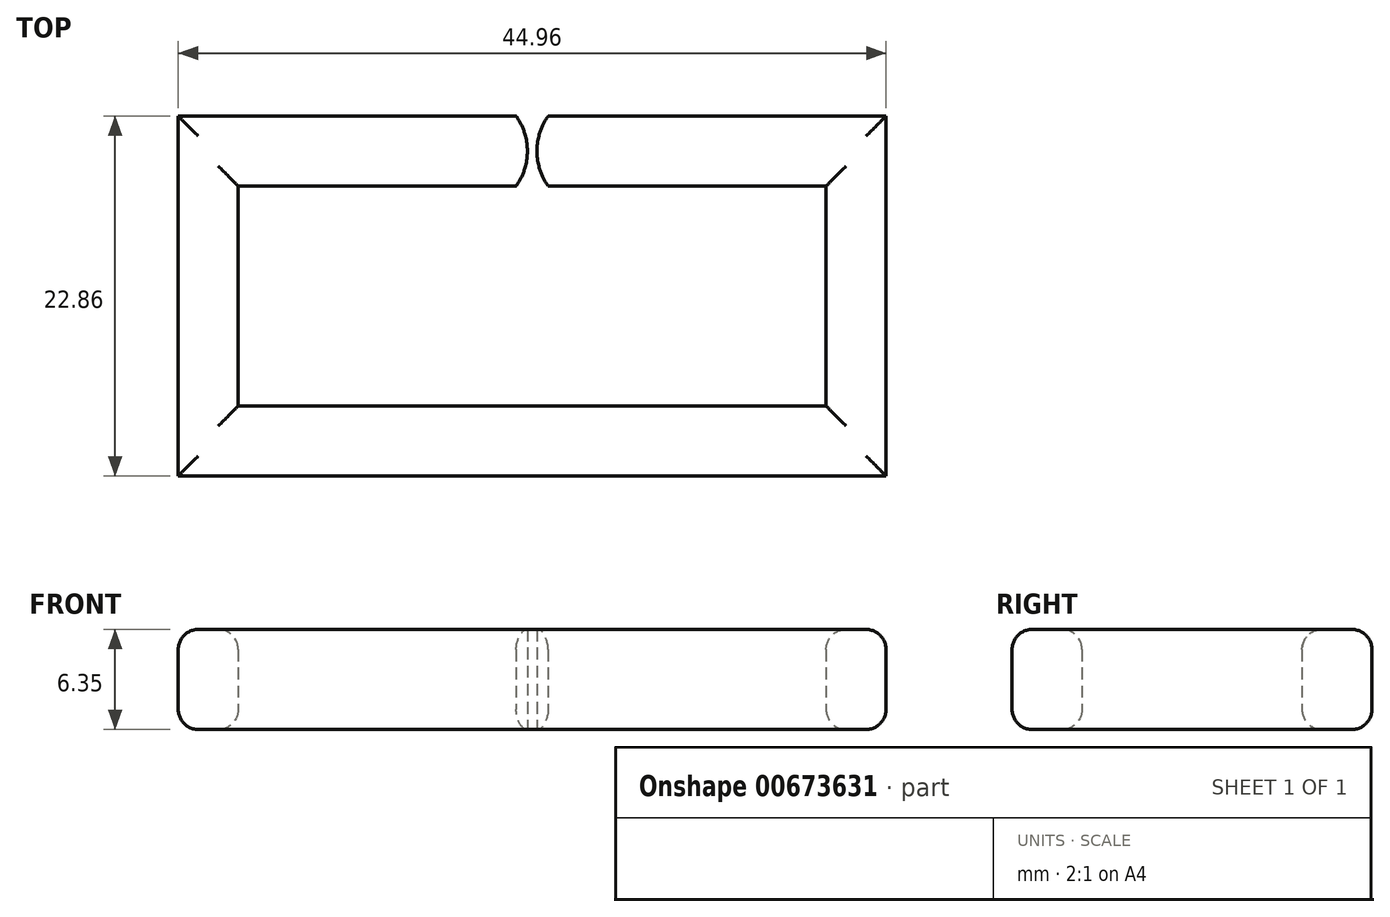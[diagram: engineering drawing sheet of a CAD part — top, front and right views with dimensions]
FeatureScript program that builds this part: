
annotation { "Feature Type Name" : "Feature", "Feature Type Description" : "" }
export const myFeature = defineFeature(function(context is Context, id is Id, definition is map)
    precondition{}
    {
        {
            var Q0;
            Q0=qCreatedBy(makeId("Top.planeOp"),FACE);
            var sketch = newSketch(context, id + "F0", { "sketchPlane" : qUnion([Q0])});
            skLineSegment(sketch, "E0.bottom", {"start": v(22.48, -11.43) * mm, "end": v(-22.48, -11.43) * mm});
            skLineSegment(sketch, "E0.top", {"start": v(22.48, 11.43) * mm, "end": v(-22.48, 11.43) * mm});
            skLineSegment(sketch, "E0.left", {"start": v(22.48, -11.43) * mm, "end": v(22.48, 11.43) * mm});
            skLineSegment(sketch, "E0.right", {"start": v(-22.48, -11.43) * mm, "end": v(-22.48, 11.43) * mm});
            skPoint(sketch, "E0.middle", {"position": v(0, 0) * mm});
            skLineSegment(sketch, "E1.bottom", {"start": v(-18.67, -6.99) * mm, "end": v(18.67, -6.99) * mm});
            skLineSegment(sketch, "E1.top", {"start": v(-18.67, 6.99) * mm, "end": v(18.67, 6.99) * mm});
            skLineSegment(sketch, "E1.left", {"start": v(-18.67, -6.99) * mm, "end": v(-18.67, 6.99) * mm});
            skLineSegment(sketch, "E1.right", {"start": v(18.67, -6.99) * mm, "end": v(18.67, 6.99) * mm});
            skLineSegment(sketch, "E2", {"start": v(0, 6.99) * mm, "end": v(0, 11.43) * mm});
            skLineSegment(sketch, "E3", {"start": v(-1.02, 11.43) * mm, "end": v(-1.02, 6.99) * mm});
            skLineSegment(sketch, "E4.MirrorCS", {"start": v(1.02, 11.43) * mm, "end": v(1.02, 6.99) * mm});
            skLineSegment(sketch, "E5.MirrorCS", {"start": v(0, 11.43) * mm, "end": v(1.02, 11.43) * mm});
            skArc(sketch, "E6", {"start": v(-1.02, 6.99) * mm, "mid": v(-0.3, 9.2) * mm, "end": v(-1.02, 11.43) * mm});
            skArc(sketch, "E7", {"start": v(1.02, 11.43) * mm, "mid": v(0.3, 9.2) * mm, "end": v(1.02, 6.99) * mm});
            skPoint(sketch, "E7.midSnap0", {"position": v(1.02, 9.2) * mm});
            skPoint(sketch, "E7.midSnap1", {"position": v(0.5, 11.43) * mm});
            skSolve(sketch);
        }
        {
            var Q0;
            Q0=makeQuery(id+"F0.imprint","IMPRINT",FACE,{"disambiguationData":[TD([[makeQuery(id+"F0.imprint","IMPRINT",EDGE,{"derivedFrom":sQuery(id+"F0.wireOp",EDGE,"E0.bottom")}),-1.0]])]});
            var Q1;
            Q1=makeQuery(id+"F0.imprint","IMPRINT",FACE,{"disambiguationData":[TD([[makeQuery(id+"F0.imprint","IMPRINT",EDGE,{"derivedFrom":sQuery(id+"F0.wireOp",EDGE,"E3")}),1.0]])]});
            var Q2;
            Q2=makeQuery(id+"F0.imprint","IMPRINT",FACE,{"disambiguationData":[TD([[makeQuery(id+"F0.imprint","IMPRINT",EDGE,{"derivedFrom":sQuery(id+"F0.wireOp",EDGE,"E4.MirrorCS")}),-1.0]])]});
            extrude(context, id + "F1", {"entities" : qUnion([Q0, Q1, Q2]), "depth" : 6.35 * mm, "offsetDistance" : 25.4 * mm});
        }
        {
            var Q0;
            {var subQ0=sQuery(id+"F0.wireOp",EDGE,"E1.top");Q0=makeQuery(id+"F1.opExtrude","CAP_EDGE",EDGE,{"disambiguationData":[OSD([subQ0]),TDD([makeQuery(id+"F0.imprint","IMPRINT",EDGE,{"disambiguationData":[TD([[makeQuery(id+"F0.imprint","INTERSECT",VERTEX,{"derivedFrom":[subQ0,sQuery(id+"F0.wireOp",EDGE,"E1.left")]}),-1.0]])],"derivedFrom":subQ0})])],"isStart":false});}
            var Q1;
            {var subQ0=sQuery(id+"F0.wireOp",EDGE,"E1.top");Q1=makeQuery(id+"F1.opExtrude","CAP_EDGE",EDGE,{"disambiguationData":[OSD([subQ0]),TDD([makeQuery(id+"F0.imprint","IMPRINT",EDGE,{"disambiguationData":[TD([[makeQuery(id+"F0.imprint","INTERSECT",VERTEX,{"derivedFrom":[subQ0,sQuery(id+"F0.wireOp",EDGE,"E1.right")]}),1.0]])],"derivedFrom":subQ0})])],"isStart":false});}
            var Q2;
            Q2=makeQuery(id+"F1.opExtrude","CAP_EDGE",EDGE,{"disambiguationData":[OSD([sQuery(id+"F0.wireOp",EDGE,"E1.right")])],"isStart":false});
            var Q3;
            Q3=makeQuery(id+"F1.opExtrude","CAP_EDGE",EDGE,{"disambiguationData":[OSD([sQuery(id+"F0.wireOp",EDGE,"E1.bottom")])],"isStart":false});
            var Q4;
            Q4=makeQuery(id+"F1.opExtrude","CAP_EDGE",EDGE,{"disambiguationData":[OSD([sQuery(id+"F0.wireOp",EDGE,"E1.left")])],"isStart":false});
            var Q5;
            Q5=makeQuery(id+"F1.opExtrude","CAP_EDGE",EDGE,{"disambiguationData":[OSD([sQuery(id+"F0.wireOp",EDGE,"E1.bottom")])],"isStart":true});
            var Q6;
            Q6=makeQuery(id+"F1.opExtrude","CAP_EDGE",EDGE,{"disambiguationData":[OSD([sQuery(id+"F0.wireOp",EDGE,"E1.right")])],"isStart":true});
            var Q7;
            {var subQ0=sQuery(id+"F0.wireOp",EDGE,"E1.top");Q7=makeQuery(id+"F1.opExtrude","CAP_EDGE",EDGE,{"disambiguationData":[OSD([subQ0]),TDD([makeQuery(id+"F0.imprint","IMPRINT",EDGE,{"disambiguationData":[TD([[makeQuery(id+"F0.imprint","INTERSECT",VERTEX,{"derivedFrom":[subQ0,sQuery(id+"F0.wireOp",EDGE,"E1.right")]}),1.0]])],"derivedFrom":subQ0})])],"isStart":true});}
            var Q8;
            {var subQ0=sQuery(id+"F0.wireOp",EDGE,"E1.top");Q8=makeQuery(id+"F1.opExtrude","CAP_EDGE",EDGE,{"disambiguationData":[OSD([subQ0]),TDD([makeQuery(id+"F0.imprint","IMPRINT",EDGE,{"disambiguationData":[TD([[makeQuery(id+"F0.imprint","INTERSECT",VERTEX,{"derivedFrom":[subQ0,sQuery(id+"F0.wireOp",EDGE,"E1.left")]}),-1.0]])],"derivedFrom":subQ0})])],"isStart":true});}
            var Q9;
            Q9=makeQuery(id+"F1.opExtrude","CAP_EDGE",EDGE,{"disambiguationData":[OSD([sQuery(id+"F0.wireOp",EDGE,"E1.left")])],"isStart":true});
            var Q10;
            {var subQ0=sQuery(id+"F0.wireOp",EDGE,"E0.top");Q10=makeQuery(id+"F1.opExtrude","CAP_EDGE",EDGE,{"disambiguationData":[OSD([subQ0]),TDD([makeQuery(id+"F0.imprint","IMPRINT",EDGE,{"disambiguationData":[TD([[makeQuery(id+"F0.imprint","INTERSECT",VERTEX,{"derivedFrom":[subQ0,sQuery(id+"F0.wireOp",EDGE,"E0.left")]}),-1.0]])],"derivedFrom":subQ0})])],"isStart":false});}
            var Q11;
            {var subQ0=sQuery(id+"F0.wireOp",EDGE,"E0.top");Q11=makeQuery(id+"F1.opExtrude","CAP_EDGE",EDGE,{"disambiguationData":[OSD([subQ0]),TDD([makeQuery(id+"F0.imprint","IMPRINT",EDGE,{"disambiguationData":[TD([[makeQuery(id+"F0.imprint","INTERSECT",VERTEX,{"derivedFrom":[subQ0,sQuery(id+"F0.wireOp",EDGE,"E0.right")]}),1.0]])],"derivedFrom":subQ0})])],"isStart":false});}
            var Q12;
            Q12=makeQuery(id+"F1.opExtrude","CAP_EDGE",EDGE,{"disambiguationData":[OSD([sQuery(id+"F0.wireOp",EDGE,"E0.right")])],"isStart":false});
            var Q13;
            Q13=makeQuery(id+"F1.opExtrude","CAP_EDGE",EDGE,{"disambiguationData":[OSD([sQuery(id+"F0.wireOp",EDGE,"E0.bottom")])],"isStart":false});
            var Q14;
            Q14=makeQuery(id+"F1.opExtrude","CAP_EDGE",EDGE,{"disambiguationData":[OSD([sQuery(id+"F0.wireOp",EDGE,"E0.left")])],"isStart":false});
            var Q15;
            Q15=makeQuery(id+"F1.opExtrude","CAP_EDGE",EDGE,{"disambiguationData":[OSD([sQuery(id+"F0.wireOp",EDGE,"E0.left")])],"isStart":true});
            var Q16;
            Q16=makeQuery(id+"F1.opExtrude","CAP_EDGE",EDGE,{"disambiguationData":[OSD([sQuery(id+"F0.wireOp",EDGE,"E0.bottom")])],"isStart":true});
            var Q17;
            {var subQ0=sQuery(id+"F0.wireOp",EDGE,"E0.top");Q17=makeQuery(id+"F1.opExtrude","CAP_EDGE",EDGE,{"disambiguationData":[OSD([subQ0]),TDD([makeQuery(id+"F0.imprint","IMPRINT",EDGE,{"disambiguationData":[TD([[makeQuery(id+"F0.imprint","INTERSECT",VERTEX,{"derivedFrom":[subQ0,sQuery(id+"F0.wireOp",EDGE,"E0.left")]}),-1.0]])],"derivedFrom":subQ0})])],"isStart":true});}
            var Q18;
            {var subQ0=sQuery(id+"F0.wireOp",EDGE,"E0.top");Q18=makeQuery(id+"F1.opExtrude","CAP_EDGE",EDGE,{"disambiguationData":[OSD([subQ0]),TDD([makeQuery(id+"F0.imprint","IMPRINT",EDGE,{"disambiguationData":[TD([[makeQuery(id+"F0.imprint","INTERSECT",VERTEX,{"derivedFrom":[subQ0,sQuery(id+"F0.wireOp",EDGE,"E0.right")]}),1.0]])],"derivedFrom":subQ0})])],"isStart":true});}
            var Q19;
            Q19=makeQuery(id+"F1.opExtrude","CAP_EDGE",EDGE,{"disambiguationData":[OSD([sQuery(id+"F0.wireOp",EDGE,"E0.right")])],"isStart":true});
            fillet(context, id + "F2", {"entities" : qUnion([Q0, Q1, Q2, Q3, Q4, Q5, Q6, Q7, Q8, Q9, Q10, Q11, Q12, Q13, Q14, Q15, Q16, Q17, Q18, Q19]), "radius" : 1.27 * mm, "tangentPropagation" : true, "allowEdgeOverflow" : false});
        }
    });
